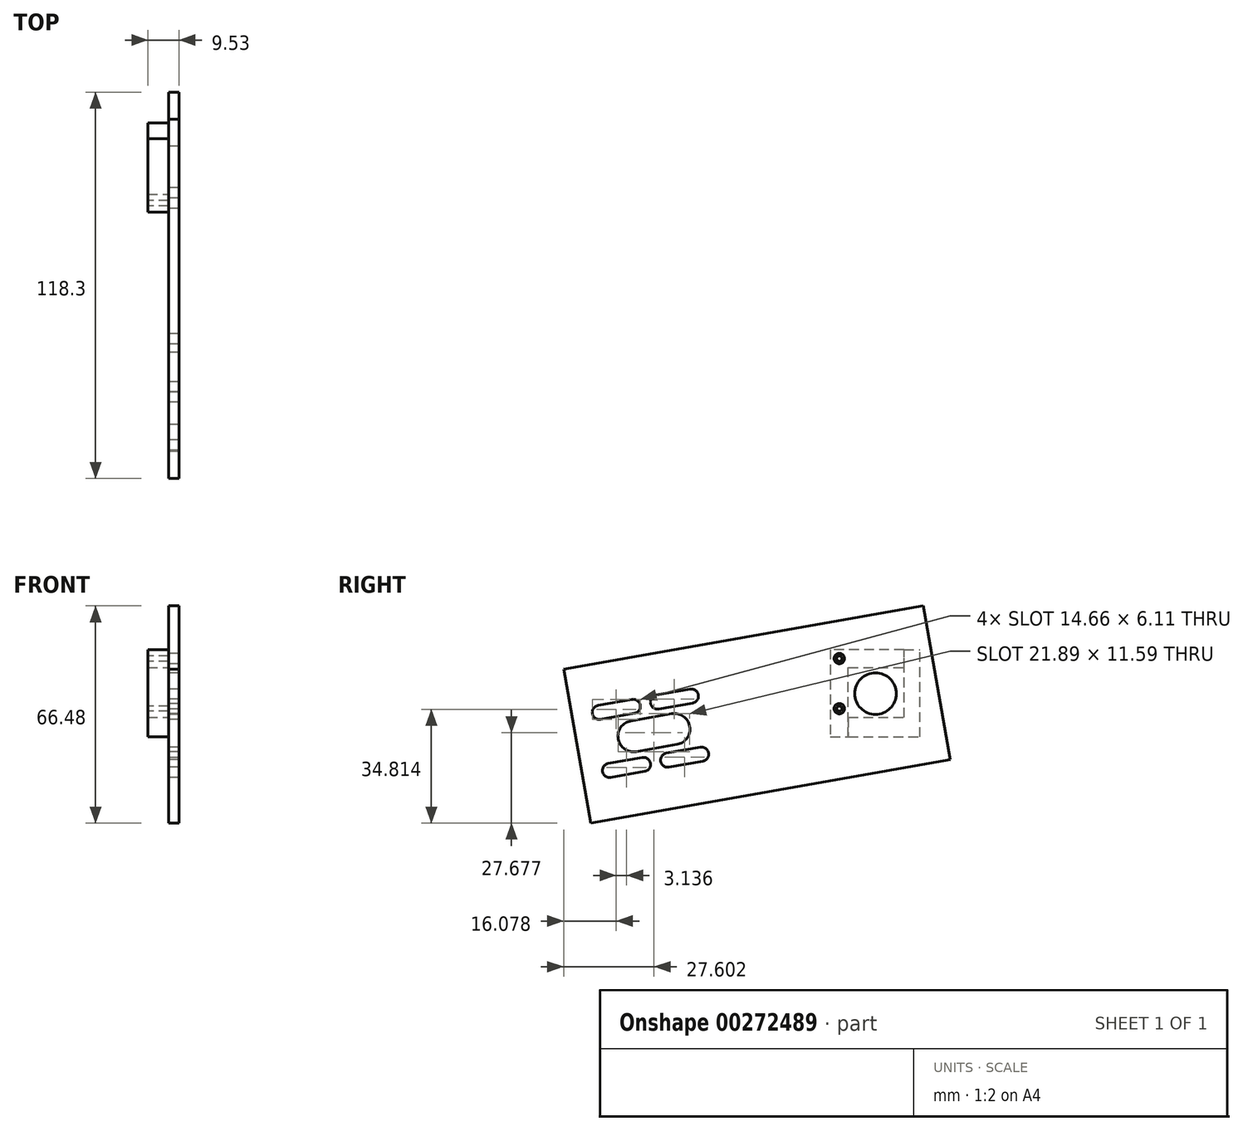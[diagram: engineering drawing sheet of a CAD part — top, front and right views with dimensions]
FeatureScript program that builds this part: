
annotation { "Feature Type Name" : "Feature", "Feature Type Description" : "" }
export const myFeature = defineFeature(function(context is Context, id is Id, definition is map)
    precondition{}
    {
        {
            var Q0;
            Q0=qCreatedBy(makeId("Right.planeOp"),FACE);
            var sketch = newSketch(context, id + "F0", { "sketchPlane" : qUnion([Q0])});
            skLineSegment(sketch, "E0", {"start": v(0, 0) * mm, "end": v(-67.79, -11.95) * mm, "construction": true});
            skLineSegment(sketch, "E1", {"start": v(0, 0) * mm, "end": v(-67.79, 0) * mm, "construction": true});
            skLineSegment(sketch, "E2", {"start": v(-67.79, 0) * mm, "end": v(-67.79, -11.95) * mm, "construction": true});
            skCircle(sketch, "E3", {"center": v(-67.79, -11.95) * mm, "radius": 4.76 * mm, "construction": true});
            skArc(sketch, "E4", {"start": v(-60.7, -15.54) * mm, "mid": v(-56.84, -10.02) * mm, "end": v(-62.36, -6.16) * mm});
            skLineSegment(sketch, "E5", {"start": v(-67.79, -11.95) * mm, "end": v(-74.04, -13.06) * mm});
            skArc(sketch, "E6", {"start": v(-74.87, -8.37) * mm, "mid": v(-78.73, -13.88) * mm, "end": v(-73.21, -17.75) * mm});
            skLineSegment(sketch, "E7", {"start": v(-74.87, -8.37) * mm, "end": v(-62.36, -6.16) * mm});
            skLineSegment(sketch, "E8", {"start": v(-73.21, -17.75) * mm, "end": v(-60.7, -15.54) * mm});
            skLineSegment(sketch, "E9", {"start": v(-78.25, -4.63) * mm, "end": v(-69.36, -3.06) * mm, "construction": true});
            skLineSegment(sketch, "E10", {"start": v(-67.79, -11.95) * mm, "end": v(-69.36, -3.06) * mm, "construction": true});
            skCircle(sketch, "E11", {"center": v(-78.25, -4.63) * mm, "radius": 2.17 * mm, "construction": true});
            skLineSegment(sketch, "E12", {"start": v(-78.25, -4.63) * mm, "end": v(-76.68, -13.52) * mm, "construction": true});
            skArc(sketch, "E13", {"start": v(-73.74, -6.04) * mm, "mid": v(-71.98, -3.52) * mm, "end": v(-74.5, -1.76) * mm});
            skLineSegment(sketch, "E14", {"start": v(-78.25, -4.63) * mm, "end": v(-84.5, -5.73) * mm, "construction": true});
            skArc(sketch, "E15", {"start": v(-84.88, -3.6) * mm, "mid": v(-86.64, -6.1) * mm, "end": v(-84.13, -7.87) * mm});
            skLineSegment(sketch, "E16", {"start": v(-84.88, -3.6) * mm, "end": v(-74.5, -1.76) * mm});
            skLineSegment(sketch, "E17", {"start": v(-84.13, -7.87) * mm, "end": v(-73.74, -6.04) * mm});
            skCircle(sketch, "E18", {"center": v(0, 0) * mm, "radius": 6.35 * mm});
            skLineSegment(sketch, "E19", {"start": v(-95.39, 7.45) * mm, "end": v(-87.09, -39.63) * mm});
            skLineSegment(sketch, "E20", {"start": v(-87.09, -39.63) * mm, "end": v(22.91, -20.23) * mm});
            skLineSegment(sketch, "E21", {"start": v(22.91, -20.23) * mm, "end": v(14.61, 26.85) * mm});
            skLineSegment(sketch, "E22", {"start": v(14.61, 26.85) * mm, "end": v(-95.39, 7.45) * mm});
            skLineSegment(sketch, "E23", {"start": v(0, 0) * mm, "end": v(18.76, 3.3) * mm});
            skLineSegment(sketch, "E24", {"start": v(-74.04, -13.06) * mm, "end": v(-82.93, -14.62) * mm, "construction": true});
            skLineSegment(sketch, "E25", {"start": v(-82.93, -14.62) * mm, "end": v(-84.5, -5.73) * mm, "construction": true});
            skCircle(sketch, "E26.MirrorC", {"center": v(-60.46, -1.5) * mm, "radius": 2.17 * mm, "construction": true});
            skArc(sketch, "E27", {"start": v(-67.1, -0.46) * mm, "mid": v(-68.86, -2.97) * mm, "end": v(-66.34, -4.73) * mm});
            skLineSegment(sketch, "E28", {"start": v(-69.36, -3.06) * mm, "end": v(-66.72, -2.6) * mm});
            skLineSegment(sketch, "E29", {"start": v(-60.46, -1.5) * mm, "end": v(-66.72, -2.6) * mm});
            skLineSegment(sketch, "E30", {"start": v(-60.46, -1.5) * mm, "end": v(-56.34, -0.76) * mm});
            skArc(sketch, "E31", {"start": v(-55.96, -2.9) * mm, "mid": v(-54.2, -0.39) * mm, "end": v(-56.71, 1.37) * mm});
            skLineSegment(sketch, "E32", {"start": v(-66.34, -4.73) * mm, "end": v(-55.96, -2.9) * mm});
            skLineSegment(sketch, "E33", {"start": v(-67.1, -0.46) * mm, "end": v(-56.71, 1.37) * mm});
            skLineSegment(sketch, "E34.MirrorCS", {"start": v(-63.96, -18.24) * mm, "end": v(-53.58, -16.41) * mm});
            skArc(sketch, "E35.MirrorCS", {"start": v(-63.2, -22.52) * mm, "mid": v(-65.72, -20.76) * mm, "end": v(-63.96, -18.24) * mm});
            skArc(sketch, "E36.MirrorCS", {"start": v(-53.58, -16.41) * mm, "mid": v(-51.06, -18.17) * mm, "end": v(-52.82, -20.69) * mm});
            skLineSegment(sketch, "E37.MirrorCS", {"start": v(-63.2, -22.52) * mm, "end": v(-52.82, -20.69) * mm});
            skLineSegment(sketch, "E38.MirrorCS", {"start": v(-81.74, -21.38) * mm, "end": v(-71.36, -19.55) * mm});
            skArc(sketch, "E39.MirrorCS", {"start": v(-71.36, -19.55) * mm, "mid": v(-68.85, -21.3) * mm, "end": v(-70.6, -23.82) * mm});
            skLineSegment(sketch, "E40.MirrorCS", {"start": v(-80.99, -25.65) * mm, "end": v(-70.6, -23.82) * mm});
            skArc(sketch, "E41.MirrorCS", {"start": v(-80.99, -25.65) * mm, "mid": v(-83.5, -23.9) * mm, "end": v(-81.74, -21.38) * mm});
            skSolve(sketch);
        }
        {
            var Q0;
            Q0 = qSketchRegion(id + "F0", true);
            var Q1;
            Q1=makeQuery(id+"F0.imprint","IMPRINT",FACE,{"disambiguationData":[TD([[makeQuery(id+"F0.imprint","IMPRINT",EDGE,{"derivedFrom":sQuery(id+"F0.wireOp",EDGE,"E4")}),-1.0]])]});
            extrude(context, id + "F1", {"entities" : qUnion([Q0, Q1]), "depth" : 3.17 * mm});
        }
        {
            var Q0;
            Q0=makeQuery(id+"F1.opExtrude","CAP_FACE",FACE,{"disambiguationData":[OSD([sQuery(id+"F0.wireOp",EDGE,"E4"),sQuery(id+"F0.wireOp",EDGE,"E6"),sQuery(id+"F0.wireOp",EDGE,"E7"),sQuery(id+"F0.wireOp",EDGE,"E8"),sQuery(id+"F0.wireOp",EDGE,"E13"),sQuery(id+"F0.wireOp",EDGE,"E15"),sQuery(id+"F0.wireOp",EDGE,"E16"),sQuery(id+"F0.wireOp",EDGE,"E17"),sQuery(id+"F0.wireOp",EDGE,"E18"),sQuery(id+"F0.wireOp",EDGE,"E19"),sQuery(id+"F0.wireOp",EDGE,"E20"),sQuery(id+"F0.wireOp",EDGE,"E21"),sQuery(id+"F0.wireOp",EDGE,"E22"),sQuery(id+"F0.wireOp",EDGE,"E27"),sQuery(id+"F0.wireOp",EDGE,"E31"),sQuery(id+"F0.wireOp",EDGE,"E32"),sQuery(id+"F0.wireOp",EDGE,"E33"),sQuery(id+"F0.wireOp",EDGE,"E34.MirrorCS"),sQuery(id+"F0.wireOp",EDGE,"E35.MirrorCS"),sQuery(id+"F0.wireOp",EDGE,"E36.MirrorCS"),sQuery(id+"F0.wireOp",EDGE,"E37.MirrorCS"),sQuery(id+"F0.wireOp",EDGE,"E38.MirrorCS"),sQuery(id+"F0.wireOp",EDGE,"E39.MirrorCS"),sQuery(id+"F0.wireOp",EDGE,"E40.MirrorCS"),sQuery(id+"F0.wireOp",EDGE,"E41.MirrorCS")])],"isStart":true});
            var sketch = newSketch(context, id + "F2", { "sketchPlane" : qUnion([Q0])});
            skLineSegment(sketch, "E42", {"start": v(8.32, -13.28) * mm, "end": v(8.32, 7.97) * mm});
            skLineSegment(sketch, "E43", {"start": v(8.32, 7.97) * mm, "end": v(-8.72, 7.97) * mm});
            skLineSegment(sketch, "E44", {"start": v(-8.72, 7.97) * mm, "end": v(-8.72, 13.48) * mm});
            skLineSegment(sketch, "E45", {"start": v(-8.72, 13.48) * mm, "end": v(13.84, 13.48) * mm});
            skLineSegment(sketch, "E46", {"start": v(13.84, 13.48) * mm, "end": v(13.84, -13.28) * mm});
            skLineSegment(sketch, "E47", {"start": v(13.84, -13.28) * mm, "end": v(8.32, -13.28) * mm});
            skSolve(sketch);
        }
        {
            var Q0;
            Q0 = qSketchRegion(id + "F2", true);
            extrude(context, id + "F3", {"entities" : qUnion([Q0]), "depth" : 6.35 * mm});
        }
        {
            var Q0;
            Q0=makeQuery(id+"F1.opExtrude","CAP_FACE",FACE,{"disambiguationData":[OSD([sQuery(id+"F0.wireOp",EDGE,"E4"),sQuery(id+"F0.wireOp",EDGE,"E6"),sQuery(id+"F0.wireOp",EDGE,"E7"),sQuery(id+"F0.wireOp",EDGE,"E8"),sQuery(id+"F0.wireOp",EDGE,"E13"),sQuery(id+"F0.wireOp",EDGE,"E15"),sQuery(id+"F0.wireOp",EDGE,"E16"),sQuery(id+"F0.wireOp",EDGE,"E17"),sQuery(id+"F0.wireOp",EDGE,"E18"),sQuery(id+"F0.wireOp",EDGE,"E19"),sQuery(id+"F0.wireOp",EDGE,"E20"),sQuery(id+"F0.wireOp",EDGE,"E21"),sQuery(id+"F0.wireOp",EDGE,"E22"),sQuery(id+"F0.wireOp",EDGE,"E27"),sQuery(id+"F0.wireOp",EDGE,"E31"),sQuery(id+"F0.wireOp",EDGE,"E32"),sQuery(id+"F0.wireOp",EDGE,"E33"),sQuery(id+"F0.wireOp",EDGE,"E34.MirrorCS"),sQuery(id+"F0.wireOp",EDGE,"E35.MirrorCS"),sQuery(id+"F0.wireOp",EDGE,"E36.MirrorCS"),sQuery(id+"F0.wireOp",EDGE,"E37.MirrorCS"),sQuery(id+"F0.wireOp",EDGE,"E38.MirrorCS"),sQuery(id+"F0.wireOp",EDGE,"E39.MirrorCS"),sQuery(id+"F0.wireOp",EDGE,"E40.MirrorCS"),sQuery(id+"F0.wireOp",EDGE,"E41.MirrorCS")])],"isStart":true});
            var sketch = newSketch(context, id + "F4", { "sketchPlane" : qUnion([Q0])});
            skLineSegment(sketch, "E48", {"start": v(-8.72, 13.48) * mm, "end": v(-13.55, 13.48) * mm});
            skLineSegment(sketch, "E49", {"start": v(8.32, -7.29) * mm, "end": v(8.32, -13.28) * mm});
            skLineSegment(sketch, "E50", {"start": v(8.32, -13.28) * mm, "end": v(-13.55, -13.28) * mm});
            skLineSegment(sketch, "E51", {"start": v(-13.55, -13.28) * mm, "end": v(-13.55, 13.48) * mm});
            skLineSegment(sketch, "E52", {"start": v(8.32, -7.29) * mm, "end": v(-8.72, -7.29) * mm});
            skLineSegment(sketch, "E53", {"start": v(-8.72, -7.29) * mm, "end": v(-8.72, 13.48) * mm});
            skSolve(sketch);
        }
        {
            var Q0;
            Q0 = qSketchRegion(id + "F4", true);
            var Q1;
            Q1=makeQuery(id+"F3.opExtrude","CAP_FACE",FACE,{"disambiguationData":[OSD([sQuery(id+"F2.wireOp",EDGE,"E42"),sQuery(id+"F2.wireOp",EDGE,"E43"),sQuery(id+"F2.wireOp",EDGE,"E44"),sQuery(id+"F2.wireOp",EDGE,"E45"),sQuery(id+"F2.wireOp",EDGE,"E46"),sQuery(id+"F2.wireOp",EDGE,"E47")])],"isStart":false});
            extrude(context, id + "F5", {"entities" : qUnion([Q0]), "endBound" : BoundingType.UP_TO_SURFACE, "endBoundEntityFace" : qUnion([Q1]), "depth" : 25.4 * mm});
        }
        {
            var Q0;
            Q0=makeQuery(id+"F3.opExtrude","CAP_FACE",FACE,{"disambiguationData":[OSD([sQuery(id+"F2.wireOp",EDGE,"E42"),sQuery(id+"F2.wireOp",EDGE,"E43"),sQuery(id+"F2.wireOp",EDGE,"E44"),sQuery(id+"F2.wireOp",EDGE,"E45"),sQuery(id+"F2.wireOp",EDGE,"E46"),sQuery(id+"F2.wireOp",EDGE,"E47")])],"isStart":false});
            var sketch = newSketch(context, id + "F6", { "sketchPlane" : qUnion([Q0])});
            skCircle(sketch, "E54", {"center": v(11.08, 10.72) * mm, "radius": 0.8 * mm});
            skCircle(sketch, "E55", {"center": v(11.08, -4.6) * mm, "radius": 0.8 * mm});
            skLineSegment(sketch, "E56", {"start": v(11.08, -13.28) * mm, "end": v(11.08, 13.48) * mm, "construction": true});
            skLineSegment(sketch, "E57", {"start": v(-8.72, 10.72) * mm, "end": v(13.84, 10.72) * mm, "construction": true});
            skSolve(sketch);
        }
        {
            var Q0;
            Q0 = qSketchRegion(id + "F6", true);
            extrude(context, id + "F7", {"entities" : qUnion([Q0]), "operationType" : NewBodyOperationType.REMOVE, "endBound" : BoundingType.THROUGH_ALL, "oppositeDirection" : true, "depth" : 25.4 * mm});
        }
        {
            var Q0;
            Q0=makeQuery(id+"F2.imprint","IMPRINT",FACE,{"disambiguationData":[TD([[makeQuery(id+"F2.imprint","IMPRINT",EDGE,{"derivedFrom":sQuery(id+"F2.wireOp",EDGE,"E42")}),1.0]])]});
            var sketch = newSketch(context, id + "F8", { "sketchPlane" : qUnion([Q0])});
            skCircle(sketch, "E58", {"center": v(11.08, 10.72) * mm, "radius": 1.59 * mm});
            skCircle(sketch, "E59", {"center": v(11.08, -4.6) * mm, "radius": 1.59 * mm});
            skSolve(sketch);
        }
        {
            var Q0;
            Q0 = qSketchRegion(id + "F8", true);
            extrude(context, id + "F9", {"entities" : qUnion([Q0]), "operationType" : NewBodyOperationType.REMOVE, "endBound" : BoundingType.THROUGH_ALL, "oppositeDirection" : true, "depth" : 25.4 * mm});
        }
    });
